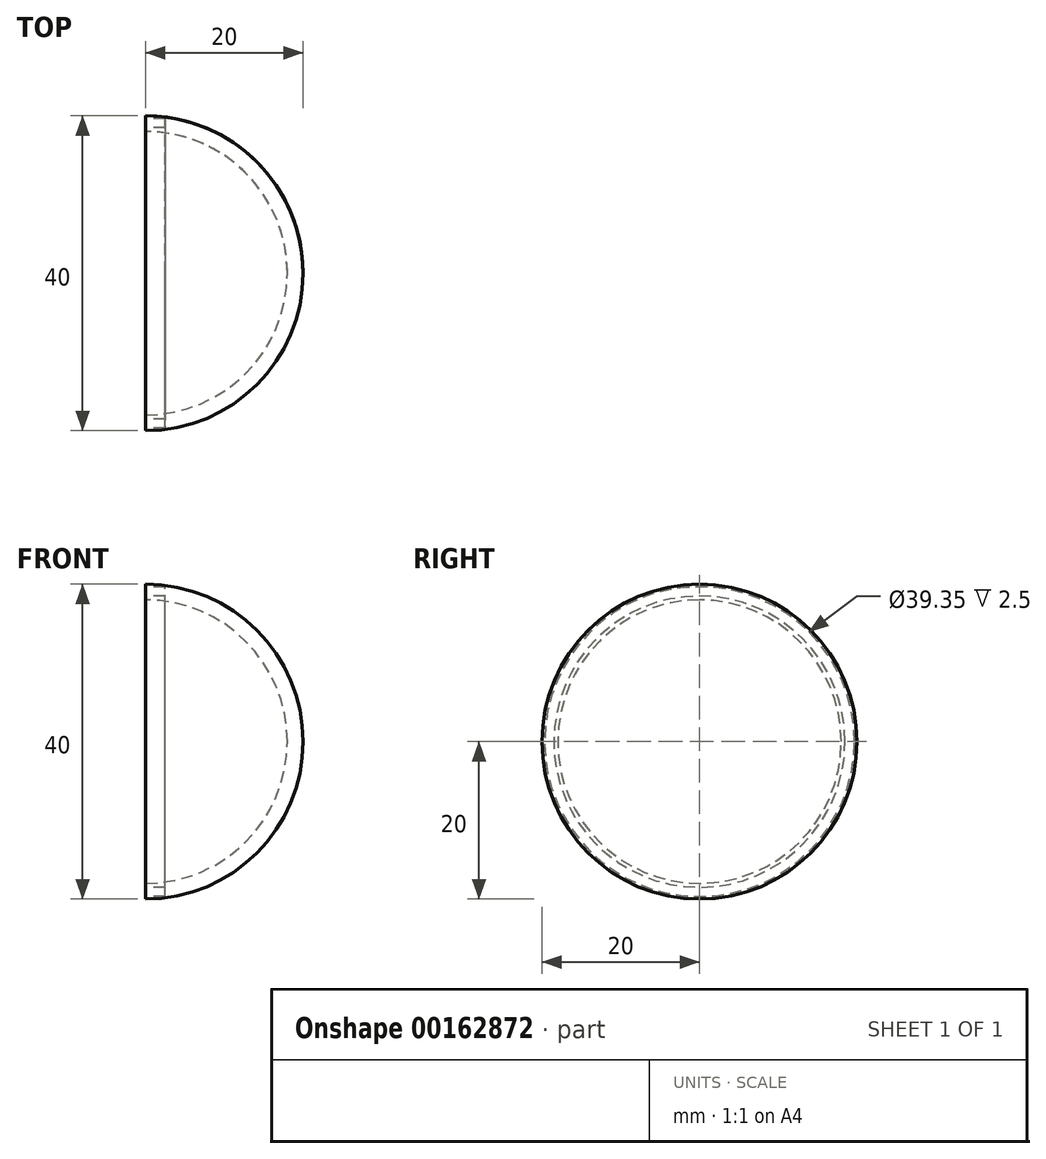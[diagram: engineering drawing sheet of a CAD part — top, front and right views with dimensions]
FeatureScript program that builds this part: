
annotation { "Feature Type Name" : "Feature", "Feature Type Description" : "" }
export const myFeature = defineFeature(function(context is Context, id is Id, definition is map)
    precondition{}
    {
        {
            var Q0;
            Q0=qCreatedBy(makeId("Top.planeOp"),FACE);
            var sketch = newSketch(context, id + "F0", { "sketchPlane" : qUnion([Q0])});
            skPoint(sketch, "E0.orphan", {"position": v(-40.66, 0) * mm});
            skArc(sketch, "E1", {"start": v(20, 0) * mm, "mid": v(14.14, 14.14) * mm, "end": v(0, 20) * mm});
            skLineSegment(sketch, "E2", {"start": v(-20, 0) * mm, "end": v(-18, 0) * mm});
            skPoint(sketch, "E3.orphan", {"position": v(-58.7, 0) * mm});
            skArc(sketch, "E4.0", {"start": v(18, 0) * mm, "mid": v(12.73, 12.73) * mm, "end": v(0, 18) * mm});
            skLineSegment(sketch, "E5.trimOffspring", {"start": v(18, 0) * mm, "end": v(20, 0) * mm});
            skLineSegment(sketch, "E6", {"start": v(-58.7, 0) * mm, "end": v(58.1, 0) * mm});
            skLineSegment(sketch, "E7.trimOffspring", {"start": v(0, 18) * mm, "end": v(0, 20) * mm});
            skPoint(sketch, "E8.start.orphan", {"position": v(0, -17.6) * mm});
            skSolve(sketch);
        }
        {
            var Q0;
            Q0 = qSketchRegion(id + "F0", true);
            var Q1;
            Q1=sQuery(id+"F0.wireOp",EDGE,"E6");
            revolve(context, id + "F1", {"entities" : qUnion([Q0]), "axis" : qUnion([Q1]), "revolveType" : RevolveType.FULL});
        }
        {
            var Q0;
            Q0=qCreatedBy(makeId("Right.planeOp"),FACE);
            var sketch = newSketch(context, id + "F2", { "sketchPlane" : qUnion([Q0])});
            skCircle(sketch, "E9", {"center": v(0, 0) * mm, "radius": 18.5 * mm});
            skCircle(sketch, "E10.0", {"center": v(0, 0) * mm, "radius": 19.68 * mm});
            skSolve(sketch);
        }
        {
            var Q0;
            Q0 = qSketchRegion(id + "F2", true);
            extrude(context, id + "F3", {"entities" : qUnion([Q0]), "operationType" : NewBodyOperationType.REMOVE, "depth" : 2.5 * mm});
        }
    });
